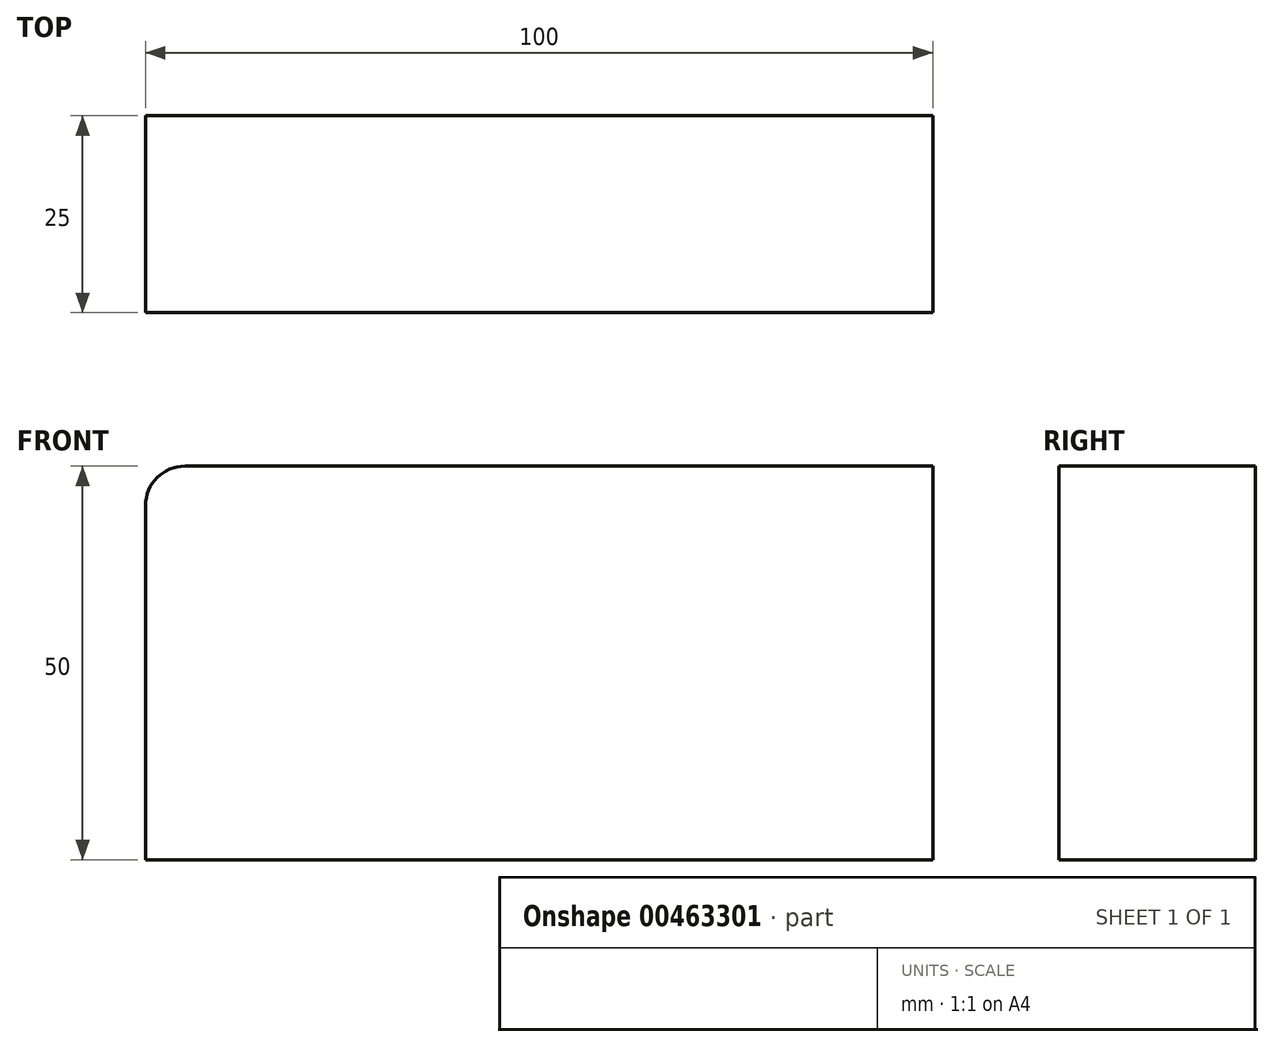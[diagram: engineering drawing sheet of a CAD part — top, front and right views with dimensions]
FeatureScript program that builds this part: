
annotation { "Feature Type Name" : "Feature", "Feature Type Description" : "" }
export const myFeature = defineFeature(function(context is Context, id is Id, definition is map)
    precondition{}
    {
        {
            var Q0;
            Q0=qCreatedBy(makeId("Front.planeOp"),FACE);
            var sketch = newSketch(context, id + "F0", { "sketchPlane" : qUnion([Q0])});
            skLineSegment(sketch, "E0.bottom", {"start": v(-52.24, 33) * mm, "end": v(42.76, 33) * mm});
            skLineSegment(sketch, "E0.top", {"start": v(-57.24, -17) * mm, "end": v(42.76, -17) * mm});
            skLineSegment(sketch, "E0.left", {"start": v(-57.24, 28) * mm, "end": v(-57.24, -17) * mm});
            skLineSegment(sketch, "E0.right", {"start": v(42.76, 33) * mm, "end": v(42.76, -17) * mm});
            skPoint(sketch, "E1.visualSharp", {"position": v(-57.24, 33) * mm});
            skArc(sketch, "E1.filletArc", {"start": v(-52.24, 33) * mm, "mid": v(-55.77, 31.55) * mm, "end": v(-57.24, 28) * mm});
            skSolve(sketch);
        }
        {
            var Q0;
            Q0=makeQuery(id+"F0.imprint","IMPRINT",FACE,{"disambiguationData":[TD([[makeQuery(id+"F0.imprint","IMPRINT",EDGE,{"derivedFrom":sQuery(id+"F0.wireOp",EDGE,"E0.bottom")}),-1.0]])]});
            extrude(context, id + "F1", {"entities" : qUnion([Q0]), "depth" : 25 * mm});
        }
    });
